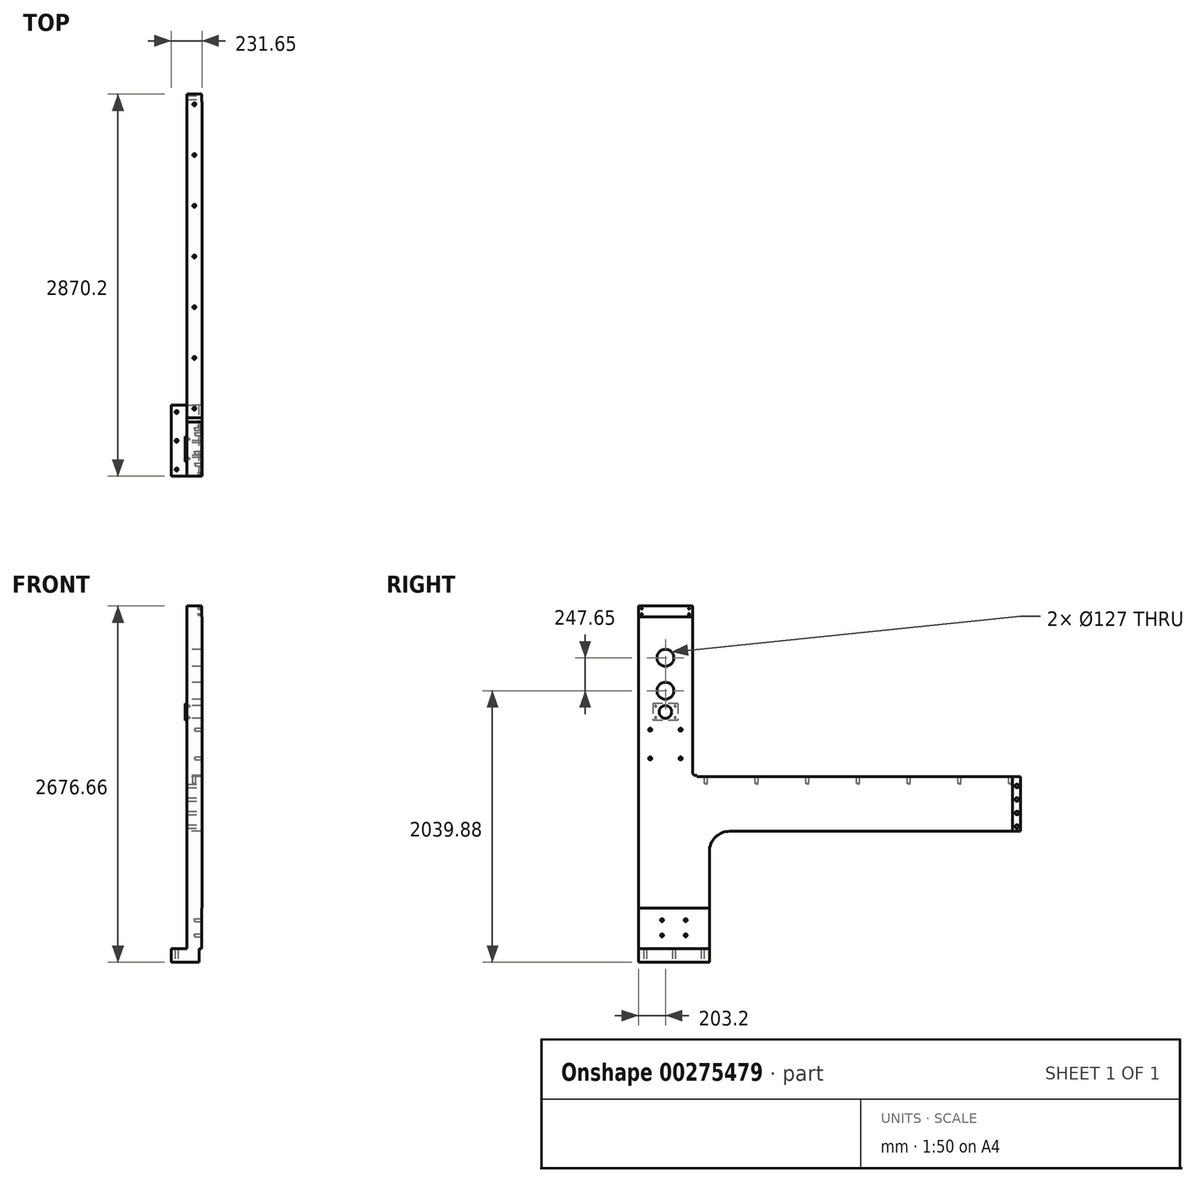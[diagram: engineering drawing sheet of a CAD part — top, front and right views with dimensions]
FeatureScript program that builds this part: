
annotation { "Feature Type Name" : "Feature", "Feature Type Description" : "" }
export const myFeature = defineFeature(function(context is Context, id is Id, definition is map)
    precondition{}
    {
        {
            var Q0;
            Q0=qCreatedBy(makeId("Right.planeOp"),FACE);
            var sketch = newSketch(context, id + "F0", { "sketchPlane" : qUnion([Q0])});
            skLineSegment(sketch, "E0", {"start": v(0, 1338.33) * mm, "end": v(0, -1338.33) * mm});
            skLineSegment(sketch, "E1.bottom", {"start": v(0, 1338.33) * mm, "end": v(406.4, 1338.33) * mm});
            skLineSegment(sketch, "E1.left", {"start": v(0, 1338.33) * mm, "end": v(0, -642.77) * mm});
            skLineSegment(sketch, "E1.right", {"start": v(406.4, 1338.33) * mm, "end": v(406.4, 90.42) * mm});
            skLineSegment(sketch, "E2", {"start": v(0, -1338.33) * mm, "end": v(2674.85, -1338.33) * mm, "construction": true});
            skLineSegment(sketch, "E3.0", {"start": v(0, -1236.73) * mm, "end": v(897.1, -1236.73) * mm, "construction": true});
            skLineSegment(sketch, "E4.bottom", {"start": v(0, -1236.73) * mm, "end": v(533.4, -1236.73) * mm});
            skLineSegment(sketch, "E4.top", {"start": v(406.4, 65.02) * mm, "end": v(438.15, 65.02) * mm});
            skLineSegment(sketch, "E4.left", {"start": v(0, -1236.73) * mm, "end": v(0, 65.02) * mm});
            skLineSegment(sketch, "E4.right", {"start": v(533.4, -1236.73) * mm, "end": v(533.4, -506.48) * mm});
            skLineSegment(sketch, "E5.bottom", {"start": v(431.8, 65.02) * mm, "end": v(438.15, 65.02) * mm});
            skLineSegment(sketch, "E5.top", {"start": v(685.8, -354.08) * mm, "end": v(2870.2, -354.08) * mm});
            skLineSegment(sketch, "E5.left", {"start": v(0, 65.02) * mm, "end": v(0, -354.08) * mm});
            skLineSegment(sketch, "E5.right", {"start": v(2870.2, 57.02) * mm, "end": v(2870.2, -354.08) * mm});
            skPoint(sketch, "E6.visualSharp", {"position": v(533.4, -354.08) * mm});
            skArc(sketch, "E6.filletArc", {"start": v(685.8, -354.08) * mm, "mid": v(578.04, -398.71) * mm, "end": v(533.4, -506.48) * mm});
            skPoint(sketch, "E7.visualSharp", {"position": v(406.4, 65.02) * mm});
            skArc(sketch, "E7.filletArc", {"start": v(406.4, 90.42) * mm, "mid": v(413.84, 72.46) * mm, "end": v(431.8, 65.02) * mm});
            skLineSegment(sketch, "E8.0", {"start": v(0, 701.55) * mm, "end": v(2674.85, 701.55) * mm, "construction": true});
            skLineSegment(sketch, "E9.0", {"start": v(0, 949.2) * mm, "end": v(2674.85, 949.2) * mm, "construction": true});
            skLineSegment(sketch, "E10", {"start": v(203.2, 1338.33) * mm, "end": v(203.2, -548.87) * mm, "construction": true});
            skCircle(sketch, "E11", {"center": v(203.2, 949.2) * mm, "radius": 63.5 * mm});
            skCircle(sketch, "E12", {"center": v(203.2, 701.55) * mm, "radius": 63.5 * mm});
            skLineSegment(sketch, "E13.0", {"start": v(438.15, 1338.33) * mm, "end": v(438.15, 701.55) * mm, "construction": true});
            skLineSegment(sketch, "E14.0", {"start": v(0, 57.02) * mm, "end": v(203.2, 57.02) * mm, "construction": true});
            skLineSegment(sketch, "E15.trimOffspring", {"start": v(438.15, 57.02) * mm, "end": v(2870.2, 57.02) * mm});
            skLineSegment(sketch, "E16.trimOffspring", {"start": v(438.15, 65.02) * mm, "end": v(438.15, 57.02) * mm});
            skSolve(sketch);
        }
        {
            var Q0;
            Q0 = qSketchRegion(id + "F0", true);
            extrude(context, id + "F1", {"entities" : qUnion([Q0]), "endBound" : BoundingType.SYMMETRIC, "depth" : 114.3 * mm});
        }
        {
            var Q0;
            Q0=makeQuery(id+"F1.opExtrude","CAP_FACE",FACE,{"disambiguationData":[OSD([sQuery(id+"F0.wireOp",EDGE,"E1.bottom"),sQuery(id+"F0.wireOp",EDGE,"E1.left"),sQuery(id+"F0.wireOp",EDGE,"E1.right"),sQuery(id+"F0.wireOp",EDGE,"E4.bottom"),sQuery(id+"F0.wireOp",EDGE,"E4.left"),sQuery(id+"F0.wireOp",EDGE,"E4.right"),sQuery(id+"F0.wireOp",EDGE,"E5.bottom"),sQuery(id+"F0.wireOp",EDGE,"E5.top"),sQuery(id+"F0.wireOp",EDGE,"E5.left"),sQuery(id+"F0.wireOp",EDGE,"E5.right"),sQuery(id+"F0.wireOp",EDGE,"E6.filletArc"),sQuery(id+"F0.wireOp",EDGE,"E7.filletArc"),sQuery(id+"F0.wireOp",EDGE,"E11"),sQuery(id+"F0.wireOp",EDGE,"E12"),sQuery(id+"F0.wireOp",EDGE,"E15.trimOffspring"),sQuery(id+"F0.wireOp",EDGE,"E16.trimOffspring")])],"isStart":false});
            var sketch = newSketch(context, id + "F2", { "sketchPlane" : qUnion([Q0])});
            skLineSegment(sketch, "E17.bottom", {"start": v(0, 1338.33) * mm, "end": v(406.4, 1338.33) * mm});
            skLineSegment(sketch, "E17.top", {"start": v(0, 1255.78) * mm, "end": v(406.4, 1255.78) * mm});
            skLineSegment(sketch, "E17.left", {"start": v(0, 1338.33) * mm, "end": v(0, 1255.78) * mm});
            skLineSegment(sketch, "E17.right", {"start": v(406.4, 1338.33) * mm, "end": v(406.4, 1255.78) * mm});
            skSolve(sketch);
        }
        {
            var Q0;
            Q0=makeQuery(id+"F2.imprint","IMPRINT",FACE,{"disambiguationData":[TD([[makeQuery(id+"F2.imprint","IMPRINT",EDGE,{"derivedFrom":sQuery(id+"F2.wireOp",EDGE,"E17.bottom")}),-1.0]])]});
            extrude(context, id + "F3", {"entities" : qUnion([Q0]), "operationType" : NewBodyOperationType.REMOVE, "oppositeDirection" : true, "depth" : 3.05 * mm});
        }
        {
            var Q0;
            Q0=makeQuery(id+"F3.boolean.opBoolean","COPY",FACE,{"derivedFrom":makeQuery(id+"F3.opExtrude","CAP_FACE",FACE,{"disambiguationData":[OSD([sQuery(id+"F2.wireOp",EDGE,"E17.bottom"),sQuery(id+"F2.wireOp",EDGE,"E17.top"),sQuery(id+"F2.wireOp",EDGE,"E17.left"),sQuery(id+"F2.wireOp",EDGE,"E17.right")])],"isStart":false})});
            var sketch = newSketch(context, id + "F4", { "sketchPlane" : qUnion([Q0])});
            skLineSegment(sketch, "E18", {"start": v(203.2, 1338.33) * mm, "end": v(203.2, 1255.78) * mm, "construction": true});
            skCircle(sketch, "E19.0", {"center": v(203.2, 949.2) * mm, "radius": 63.5 * mm, "construction": true});
            skLineSegment(sketch, "E20", {"start": v(203.2, 949.2) * mm, "end": v(580.51, 949.2) * mm, "construction": true});
            skLineSegment(sketch, "E21.0", {"start": v(25.4, 1276.22) * mm, "end": v(580.51, 1276.22) * mm, "construction": true});
            skLineSegment(sketch, "E22.0", {"start": v(25.4, 1320.67) * mm, "end": v(580.51, 1320.67) * mm, "construction": true});
            skLineSegment(sketch, "E23.0", {"start": v(25.4, 1338.33) * mm, "end": v(25.4, 1255.78) * mm, "construction": true});
            skPoint(sketch, "E24", {"position": v(25.4, 1320.67) * mm});
            skPoint(sketch, "E25", {"position": v(25.4, 1276.22) * mm});
            skPoint(sketch, "E26.MirrorP", {"position": v(381, 1320.67) * mm});
            skPoint(sketch, "E27.MirrorP", {"position": v(381, 1276.22) * mm});
            skSolve(sketch);
        }
        {
            var Q0;
            Q0=sQuery(id+"F4.wireOp",VERTEX,"E24");
            var Q1;
            Q1=sQuery(id+"F4.wireOp",VERTEX,"E25");
            var Q2;
            Q2=sQuery(id+"F4.wireOp",VERTEX,"E26.MirrorP");
            var Q3;
            Q3=sQuery(id+"F4.wireOp",VERTEX,"E27.MirrorP");
            var Q4;
            Q4=makeQuery(id+"F1.opExtrude","SWEPT_BODY",BODY,{"disambiguationData":[OSD([sQuery(id+"F0.wireOp",EDGE,"E1.bottom"),sQuery(id+"F0.wireOp",EDGE,"E1.left"),sQuery(id+"F0.wireOp",EDGE,"E1.right"),sQuery(id+"F0.wireOp",EDGE,"E4.bottom"),sQuery(id+"F0.wireOp",EDGE,"E4.left"),sQuery(id+"F0.wireOp",EDGE,"E4.right"),sQuery(id+"F0.wireOp",EDGE,"E5.bottom"),sQuery(id+"F0.wireOp",EDGE,"E5.top"),sQuery(id+"F0.wireOp",EDGE,"E5.left"),sQuery(id+"F0.wireOp",EDGE,"E5.right"),sQuery(id+"F0.wireOp",EDGE,"E6.filletArc"),sQuery(id+"F0.wireOp",EDGE,"E7.filletArc"),sQuery(id+"F0.wireOp",EDGE,"E11"),sQuery(id+"F0.wireOp",EDGE,"E12"),sQuery(id+"F0.wireOp",EDGE,"E15.trimOffspring"),sQuery(id+"F0.wireOp",EDGE,"E16.trimOffspring")])]});
            hole(context, id + "F5", {"style" : HoleStyle.SIMPLE, "endStyle" : HoleEndStyle.BLIND, "standardTappedOrClearance" : lookupTablePath({ "standard" : "ANSI", "engagement" : "75%", "pitch" : "13 tpi", "size" : "1/2", "type" : "Tapped" }), "standardBlindInLast" : lookupTablePath({ "standard" : "ANSI", "engagement" : "75%", "pitch" : "13 tpi", "size" : "1/2", "type" : "Tapped" }), "holeDiameter" : 10.72 * mm, "showTappedDepth" : true, "holeDepth" : 25.4 * mm, "tappedDepth" : 19.54 * mm, "tapClearance" : 3, "startFromSketch" : true, "locations" : qUnion([Q0, Q1, Q2, Q3]), "scope" : qUnion([Q4]), "majorDiameter" : 12.7 * mm});
        }
        {
            var Q0;
            Q0=makeQuery(id+"F1.opExtrude","CAP_FACE",FACE,{"disambiguationData":[OSD([sQuery(id+"F0.wireOp",EDGE,"E1.bottom"),sQuery(id+"F0.wireOp",EDGE,"E1.left"),sQuery(id+"F0.wireOp",EDGE,"E1.right"),sQuery(id+"F0.wireOp",EDGE,"E4.bottom"),sQuery(id+"F0.wireOp",EDGE,"E4.left"),sQuery(id+"F0.wireOp",EDGE,"E4.right"),sQuery(id+"F0.wireOp",EDGE,"E5.bottom"),sQuery(id+"F0.wireOp",EDGE,"E5.top"),sQuery(id+"F0.wireOp",EDGE,"E5.left"),sQuery(id+"F0.wireOp",EDGE,"E5.right"),sQuery(id+"F0.wireOp",EDGE,"E6.filletArc"),sQuery(id+"F0.wireOp",EDGE,"E7.filletArc"),sQuery(id+"F0.wireOp",EDGE,"E11"),sQuery(id+"F0.wireOp",EDGE,"E12"),sQuery(id+"F0.wireOp",EDGE,"E15.trimOffspring"),sQuery(id+"F0.wireOp",EDGE,"E16.trimOffspring")])],"isStart":true});
            var sketch = newSketch(context, id + "F6", { "sketchPlane" : qUnion([Q0])});
            skCircle(sketch, "E28.0", {"center": v(-203.2, 949.2) * mm, "radius": 63.5 * mm, "construction": true});
            skCircle(sketch, "E29.0", {"center": v(-203.2, 701.55) * mm, "radius": 63.5 * mm, "construction": true});
            skCircle(sketch, "E30", {"center": v(-203.2, 949.2) * mm, "radius": 104.78 * mm});
            skCircle(sketch, "E31", {"center": v(-203.2, 701.55) * mm, "radius": 104.78 * mm});
            skSolve(sketch);
        }
        {
            var Q0;
            Q0=makeQuery(id+"F1.opExtrude","CAP_FACE",FACE,{"disambiguationData":[OSD([sQuery(id+"F0.wireOp",EDGE,"E1.bottom"),sQuery(id+"F0.wireOp",EDGE,"E1.left"),sQuery(id+"F0.wireOp",EDGE,"E1.right"),sQuery(id+"F0.wireOp",EDGE,"E4.bottom"),sQuery(id+"F0.wireOp",EDGE,"E4.left"),sQuery(id+"F0.wireOp",EDGE,"E4.right"),sQuery(id+"F0.wireOp",EDGE,"E5.bottom"),sQuery(id+"F0.wireOp",EDGE,"E5.top"),sQuery(id+"F0.wireOp",EDGE,"E5.left"),sQuery(id+"F0.wireOp",EDGE,"E5.right"),sQuery(id+"F0.wireOp",EDGE,"E6.filletArc"),sQuery(id+"F0.wireOp",EDGE,"E7.filletArc"),sQuery(id+"F0.wireOp",EDGE,"E11"),sQuery(id+"F0.wireOp",EDGE,"E12"),sQuery(id+"F0.wireOp",EDGE,"E15.trimOffspring"),sQuery(id+"F0.wireOp",EDGE,"E16.trimOffspring")])],"isStart":false});
            var sketch = newSketch(context, id + "F7", { "sketchPlane" : qUnion([Q0])});
            skCircle(sketch, "E32.0", {"center": v(203.2, 701.55) * mm, "radius": 63.5 * mm, "construction": true});
            skLineSegment(sketch, "E33", {"start": v(203.2, 701.55) * mm, "end": v(203.2, -117.25) * mm, "construction": true});
            skLineSegment(sketch, "E34", {"start": v(203.2, 701.55) * mm, "end": v(767.73, 701.55) * mm, "construction": true});
            skLineSegment(sketch, "E35.0", {"start": v(203.2, 409.45) * mm, "end": v(767.73, 409.45) * mm, "construction": true});
            skLineSegment(sketch, "E36.0", {"start": v(203.2, 193.55) * mm, "end": v(767.73, 193.55) * mm, "construction": true});
            skLineSegment(sketch, "E37.0", {"start": v(317.5, 701.55) * mm, "end": v(317.5, -117.25) * mm, "construction": true});
            skPoint(sketch, "E38", {"position": v(317.5, 409.45) * mm});
            skPoint(sketch, "E39", {"position": v(317.5, 193.55) * mm});
            skPoint(sketch, "E40.MirrorP", {"position": v(88.9, 409.45) * mm});
            skPoint(sketch, "E41.MirrorP", {"position": v(88.9, 193.55) * mm});
            skSolve(sketch);
        }
        {
            var Q0;
            Q0=sQuery(id+"F7.wireOp",VERTEX,"E40.MirrorP");
            var Q1;
            Q1=sQuery(id+"F7.wireOp",VERTEX,"E38");
            var Q2;
            Q2=sQuery(id+"F7.wireOp",VERTEX,"E41.MirrorP");
            var Q3;
            Q3=sQuery(id+"F7.wireOp",VERTEX,"E39");
            var Q4;
            Q4=makeQuery(id+"F1.opExtrude","SWEPT_BODY",BODY,{"disambiguationData":[OSD([sQuery(id+"F0.wireOp",EDGE,"E1.bottom"),sQuery(id+"F0.wireOp",EDGE,"E1.left"),sQuery(id+"F0.wireOp",EDGE,"E1.right"),sQuery(id+"F0.wireOp",EDGE,"E4.bottom"),sQuery(id+"F0.wireOp",EDGE,"E4.left"),sQuery(id+"F0.wireOp",EDGE,"E4.right"),sQuery(id+"F0.wireOp",EDGE,"E5.bottom"),sQuery(id+"F0.wireOp",EDGE,"E5.top"),sQuery(id+"F0.wireOp",EDGE,"E5.left"),sQuery(id+"F0.wireOp",EDGE,"E5.right"),sQuery(id+"F0.wireOp",EDGE,"E6.filletArc"),sQuery(id+"F0.wireOp",EDGE,"E7.filletArc"),sQuery(id+"F0.wireOp",EDGE,"E11"),sQuery(id+"F0.wireOp",EDGE,"E12"),sQuery(id+"F0.wireOp",EDGE,"E15.trimOffspring"),sQuery(id+"F0.wireOp",EDGE,"E16.trimOffspring")])]});
            hole(context, id + "F8", {"style" : HoleStyle.SIMPLE, "endStyle" : HoleEndStyle.BLIND, "standardTappedOrClearance" : lookupTablePath({ "standard" : "ANSI", "engagement" : "75%", "pitch" : "8 tpi", "size" : "1", "type" : "Tapped" }), "standardBlindInLast" : lookupTablePath({ "standard" : "ANSI", "engagement" : "75%", "pitch" : "8 tpi", "size" : "1", "type" : "Tapped" }), "holeDiameter" : 22.22 * mm, "showTappedDepth" : true, "holeDepth" : 50.8 * mm, "tappedDepth" : 41.27 * mm, "tapClearance" : 3, "startFromSketch" : true, "locations" : qUnion([Q0, Q1, Q2, Q3]), "scope" : qUnion([Q4]), "majorDiameter" : 25.4 * mm});
        }
        {
            var Q0;
            Q0=makeQuery(id+"F1.opExtrude","CAP_FACE",FACE,{"disambiguationData":[OSD([sQuery(id+"F0.wireOp",EDGE,"E1.bottom"),sQuery(id+"F0.wireOp",EDGE,"E1.left"),sQuery(id+"F0.wireOp",EDGE,"E1.right"),sQuery(id+"F0.wireOp",EDGE,"E4.bottom"),sQuery(id+"F0.wireOp",EDGE,"E4.left"),sQuery(id+"F0.wireOp",EDGE,"E4.right"),sQuery(id+"F0.wireOp",EDGE,"E5.bottom"),sQuery(id+"F0.wireOp",EDGE,"E5.top"),sQuery(id+"F0.wireOp",EDGE,"E5.left"),sQuery(id+"F0.wireOp",EDGE,"E5.right"),sQuery(id+"F0.wireOp",EDGE,"E6.filletArc"),sQuery(id+"F0.wireOp",EDGE,"E7.filletArc"),sQuery(id+"F0.wireOp",EDGE,"E11"),sQuery(id+"F0.wireOp",EDGE,"E12"),sQuery(id+"F0.wireOp",EDGE,"E15.trimOffspring"),sQuery(id+"F0.wireOp",EDGE,"E16.trimOffspring")])],"isStart":false});
            var sketch = newSketch(context, id + "F9", { "sketchPlane" : qUnion([Q0])});
            skLineSegment(sketch, "E42.bottom", {"start": v(2870.2, 57.02) * mm, "end": v(2813.05, 57.02) * mm});
            skLineSegment(sketch, "E42.top", {"start": v(2870.2, -354.08) * mm, "end": v(2813.05, -354.08) * mm});
            skLineSegment(sketch, "E42.left", {"start": v(2870.2, 57.02) * mm, "end": v(2870.2, -354.08) * mm});
            skLineSegment(sketch, "E42.right", {"start": v(2813.05, 57.02) * mm, "end": v(2813.05, -354.08) * mm});
            skSolve(sketch);
        }
        {
            var Q0;
            Q0 = qSketchRegion(id + "F9", true);
            extrude(context, id + "F10", {"entities" : qUnion([Q0]), "operationType" : NewBodyOperationType.REMOVE, "oppositeDirection" : true, "depth" : 3.17 * mm});
        }
        {
            var Q0;
            Q0=makeQuery(id+"F10.boolean.opBoolean","COPY",FACE,{"derivedFrom":makeQuery(id+"F10.opExtrude","CAP_FACE",FACE,{"disambiguationData":[OSD([sQuery(id+"F9.wireOp",EDGE,"E42.bottom"),sQuery(id+"F9.wireOp",EDGE,"E42.top"),sQuery(id+"F9.wireOp",EDGE,"E42.left"),sQuery(id+"F9.wireOp",EDGE,"E42.right")])],"isStart":false})});
            var sketch = newSketch(context, id + "F11", { "sketchPlane" : qUnion([Q0])});
            skLineSegment(sketch, "E43.0", {"start": v(2813.05, 57.02) * mm, "end": v(2870.2, 57.02) * mm, "construction": true});
            skCircle(sketch, "E44.0", {"center": v(203.2, 701.55) * mm, "radius": 63.5 * mm, "construction": true});
            skLineSegment(sketch, "E45", {"start": v(203.2, 701.55) * mm, "end": v(203.2, -538.92) * mm, "construction": true});
            skLineSegment(sketch, "E46.0", {"start": v(2844.8, 701.55) * mm, "end": v(2844.8, -538.92) * mm, "construction": true});
            skLineSegment(sketch, "E47.0", {"start": v(2813.05, -12.83) * mm, "end": v(2870.2, -12.83) * mm, "construction": true});
            skPoint(sketch, "E48", {"position": v(2844.8, -12.83) * mm});
            skPoint(sketch, "E49.0.1.0", {"position": v(2844.8, -114.43) * mm});
            skPoint(sketch, "E49.0.2.0", {"position": v(2844.8, -216.03) * mm});
            skPoint(sketch, "E49.0.3.0", {"position": v(2844.8, -317.63) * mm});
            skLineSegment(sketch, "E49.direction1", {"start": v(2844.8, -12.83) * mm, "end": v(2870.2, -12.83) * mm, "construction": true});
            skLineSegment(sketch, "E49.direction2", {"start": v(2844.8, -12.83) * mm, "end": v(2844.8, -114.43) * mm, "construction": true});
            skSolve(sketch);
        }
        {
            var Q0;
            Q0=sQuery(id+"F11.wireOp",VERTEX,"E48");
            var Q1;
            Q1=sQuery(id+"F11.wireOp",VERTEX,"E49.0.1.0");
            var Q2;
            Q2=sQuery(id+"F11.wireOp",VERTEX,"E49.0.2.0");
            var Q3;
            Q3=sQuery(id+"F11.wireOp",VERTEX,"E49.0.3.0");
            var Q4;
            Q4=makeQuery(id+"F1.opExtrude","SWEPT_BODY",BODY,{"disambiguationData":[OSD([sQuery(id+"F0.wireOp",EDGE,"E1.bottom"),sQuery(id+"F0.wireOp",EDGE,"E1.left"),sQuery(id+"F0.wireOp",EDGE,"E1.right"),sQuery(id+"F0.wireOp",EDGE,"E4.bottom"),sQuery(id+"F0.wireOp",EDGE,"E4.left"),sQuery(id+"F0.wireOp",EDGE,"E4.right"),sQuery(id+"F0.wireOp",EDGE,"E5.bottom"),sQuery(id+"F0.wireOp",EDGE,"E5.top"),sQuery(id+"F0.wireOp",EDGE,"E5.left"),sQuery(id+"F0.wireOp",EDGE,"E5.right"),sQuery(id+"F0.wireOp",EDGE,"E6.filletArc"),sQuery(id+"F0.wireOp",EDGE,"E7.filletArc"),sQuery(id+"F0.wireOp",EDGE,"E11"),sQuery(id+"F0.wireOp",EDGE,"E12"),sQuery(id+"F0.wireOp",EDGE,"E15.trimOffspring"),sQuery(id+"F0.wireOp",EDGE,"E16.trimOffspring")])]});
            hole(context, id + "F12", {"style" : HoleStyle.SIMPLE, "endStyle" : HoleEndStyle.THROUGH, "holeDiameter" : 26.92 * mm, "tappedDepth" : 41.27 * mm, "tapClearance" : 3, "startFromSketch" : true, "locations" : qUnion([Q0, Q1, Q2, Q3]), "scope" : qUnion([Q4])});
        }
        {
            var Q0;
            Q0=makeQuery(id+"F1.opExtrude","SWEPT_FACE",FACE,{"disambiguationData":[OSD([sQuery(id+"F0.wireOp",EDGE,"E15.trimOffspring")])]});
            var sketch = newSketch(context, id + "F13", { "sketchPlane" : qUnion([Q0])});
            skLineSegment(sketch, "E50", {"start": v(0, -474.51) * mm, "end": v(0, 3159.2) * mm, "construction": true});
            skLineSegment(sketch, "E51.0", {"start": v(-31.75, 98.43) * mm, "end": v(-31.75, 307.98) * mm, "construction": true});
            skLineSegment(sketch, "E52", {"start": v(-31.75, 203.2) * mm, "end": v(158.49, 203.2) * mm, "construction": true});
            skLineSegment(sketch, "E53.0", {"start": v(-31.75, 508) * mm, "end": v(158.49, 508) * mm, "construction": true});
            skPoint(sketch, "E54", {"position": v(0, 508) * mm});
            skPoint(sketch, "E55.0.1.0", {"position": v(0, 889) * mm});
            skPoint(sketch, "E55.0.2.0", {"position": v(0, 1270) * mm});
            skPoint(sketch, "E55.0.3.0", {"position": v(0, 1651) * mm});
            skPoint(sketch, "E55.0.4.0", {"position": v(0, 2032) * mm});
            skPoint(sketch, "E55.0.5.0", {"position": v(0, 2413) * mm});
            skPoint(sketch, "E55.0.6.0", {"position": v(0, 2794) * mm});
            skLineSegment(sketch, "E55.direction1", {"start": v(0, 508) * mm, "end": v(25.4, 508) * mm, "construction": true});
            skLineSegment(sketch, "E55.direction2", {"start": v(0, 508) * mm, "end": v(0, 889) * mm, "construction": true});
            skSolve(sketch);
        }
        {
            var Q0;
            Q0=sQuery(id+"F13.wireOp",VERTEX,"E54");
            var Q1;
            Q1=sQuery(id+"F13.wireOp",VERTEX,"E55.0.1.0");
            var Q2;
            Q2=sQuery(id+"F13.wireOp",VERTEX,"E55.0.2.0");
            var Q3;
            Q3=sQuery(id+"F13.wireOp",VERTEX,"E55.0.3.0");
            var Q4;
            Q4=sQuery(id+"F13.wireOp",VERTEX,"E55.0.4.0");
            var Q5;
            Q5=sQuery(id+"F13.wireOp",VERTEX,"E55.0.5.0");
            var Q6;
            Q6=sQuery(id+"F13.wireOp",VERTEX,"E55.0.6.0");
            var Q7;
            Q7=makeQuery(id+"F1.opExtrude","SWEPT_BODY",BODY,{"disambiguationData":[OSD([sQuery(id+"F0.wireOp",EDGE,"E1.bottom"),sQuery(id+"F0.wireOp",EDGE,"E1.left"),sQuery(id+"F0.wireOp",EDGE,"E1.right"),sQuery(id+"F0.wireOp",EDGE,"E4.bottom"),sQuery(id+"F0.wireOp",EDGE,"E4.left"),sQuery(id+"F0.wireOp",EDGE,"E4.right"),sQuery(id+"F0.wireOp",EDGE,"E5.bottom"),sQuery(id+"F0.wireOp",EDGE,"E5.top"),sQuery(id+"F0.wireOp",EDGE,"E5.left"),sQuery(id+"F0.wireOp",EDGE,"E5.right"),sQuery(id+"F0.wireOp",EDGE,"E6.filletArc"),sQuery(id+"F0.wireOp",EDGE,"E7.filletArc"),sQuery(id+"F0.wireOp",EDGE,"E11"),sQuery(id+"F0.wireOp",EDGE,"E12"),sQuery(id+"F0.wireOp",EDGE,"E15.trimOffspring"),sQuery(id+"F0.wireOp",EDGE,"E16.trimOffspring")])]});
            hole(context, id + "F14", {"style" : HoleStyle.SIMPLE, "endStyle" : HoleEndStyle.BLIND, "standardTappedOrClearance" : lookupTablePath({ "standard" : "ANSI", "engagement" : "75%", "pitch" : "8 tpi", "size" : "1", "type" : "Tapped" }), "standardBlindInLast" : lookupTablePath({ "standard" : "ANSI", "engagement" : "75%", "pitch" : "8 tpi", "size" : "1", "type" : "Tapped" }), "holeDiameter" : 22.22 * mm, "showTappedDepth" : true, "holeDepth" : 50.8 * mm, "tappedDepth" : 41.27 * mm, "tapClearance" : 3, "startFromSketch" : true, "locations" : qUnion([Q0, Q1, Q2, Q3, Q4, Q5, Q6]), "scope" : qUnion([Q7]), "majorDiameter" : 25.4 * mm});
        }
        {
            var Q0;
            Q0=makeQuery(id+"F1.opExtrude","CAP_FACE",FACE,{"disambiguationData":[OSD([sQuery(id+"F0.wireOp",EDGE,"E1.bottom"),sQuery(id+"F0.wireOp",EDGE,"E1.left"),sQuery(id+"F0.wireOp",EDGE,"E1.right"),sQuery(id+"F0.wireOp",EDGE,"E4.bottom"),sQuery(id+"F0.wireOp",EDGE,"E4.left"),sQuery(id+"F0.wireOp",EDGE,"E4.right"),sQuery(id+"F0.wireOp",EDGE,"E5.bottom"),sQuery(id+"F0.wireOp",EDGE,"E5.top"),sQuery(id+"F0.wireOp",EDGE,"E5.left"),sQuery(id+"F0.wireOp",EDGE,"E5.right"),sQuery(id+"F0.wireOp",EDGE,"E6.filletArc"),sQuery(id+"F0.wireOp",EDGE,"E7.filletArc"),sQuery(id+"F0.wireOp",EDGE,"E11"),sQuery(id+"F0.wireOp",EDGE,"E12"),sQuery(id+"F0.wireOp",EDGE,"E15.trimOffspring"),sQuery(id+"F0.wireOp",EDGE,"E16.trimOffspring")])],"isStart":false});
            var sketch = newSketch(context, id + "F15", { "sketchPlane" : qUnion([Q0])});
            skLineSegment(sketch, "E56.bottom", {"start": v(0, -1236.73) * mm, "end": v(533.4, -1236.73) * mm});
            skLineSegment(sketch, "E56.top", {"start": v(0, -931.93) * mm, "end": v(533.4, -931.93) * mm});
            skLineSegment(sketch, "E56.left", {"start": v(0, -1236.73) * mm, "end": v(0, -931.93) * mm});
            skLineSegment(sketch, "E56.right", {"start": v(533.4, -1236.73) * mm, "end": v(533.4, -931.93) * mm});
            skSolve(sketch);
        }
        {
            var Q0;
            Q0=makeQuery(id+"F15.imprint","IMPRINT",FACE,{"disambiguationData":[TD([[makeQuery(id+"F15.imprint","IMPRINT",EDGE,{"derivedFrom":sQuery(id+"F15.wireOp",EDGE,"E56.bottom")}),1.0]])]});
            extrude(context, id + "F16", {"entities" : qUnion([Q0]), "operationType" : NewBodyOperationType.REMOVE, "oppositeDirection" : true, "depth" : 3.05 * mm});
        }
        {
            var Q0;
            Q0=makeQuery(id+"F16.boolean.opBoolean","COPY",FACE,{"derivedFrom":makeQuery(id+"F16.opExtrude","CAP_FACE",FACE,{"disambiguationData":[OSD([sQuery(id+"F15.wireOp",EDGE,"E56.bottom"),sQuery(id+"F15.wireOp",EDGE,"E56.top"),sQuery(id+"F15.wireOp",EDGE,"E56.left"),sQuery(id+"F15.wireOp",EDGE,"E56.right")])],"isStart":false})});
            var sketch = newSketch(context, id + "F17", { "sketchPlane" : qUnion([Q0])});
            skLineSegment(sketch, "E57.0", {"start": v(0, -1236.73) * mm, "end": v(533.4, -1236.73) * mm, "construction": true});
            skLineSegment(sketch, "E58", {"start": v(266.7, -1236.73) * mm, "end": v(266.7, -931.93) * mm, "construction": true});
            skLineSegment(sketch, "E59.0", {"start": v(0, -1135.13) * mm, "end": v(533.4, -1135.13) * mm, "construction": true});
            skLineSegment(sketch, "E60.0", {"start": v(0, -1020.83) * mm, "end": v(533.4, -1020.83) * mm, "construction": true});
            skLineSegment(sketch, "E61.0", {"start": v(177.8, -1236.73) * mm, "end": v(177.8, -931.93) * mm, "construction": true});
            skPoint(sketch, "E62", {"position": v(177.8, -1020.83) * mm});
            skPoint(sketch, "E63", {"position": v(177.8, -1135.13) * mm});
            skPoint(sketch, "E64.MirrorP", {"position": v(355.6, -1020.83) * mm});
            skPoint(sketch, "E65.MirrorP", {"position": v(355.6, -1135.13) * mm});
            skSolve(sketch);
        }
        {
            var Q0;
            Q0=sQuery(id+"F17.wireOp",VERTEX,"E62");
            var Q1;
            Q1=sQuery(id+"F17.wireOp",VERTEX,"E64.MirrorP");
            var Q2;
            Q2=sQuery(id+"F17.wireOp",VERTEX,"E65.MirrorP");
            var Q3;
            Q3=sQuery(id+"F17.wireOp",VERTEX,"E63");
            var Q4;
            Q4=makeQuery(id+"F1.opExtrude","SWEPT_BODY",BODY,{"disambiguationData":[OSD([sQuery(id+"F0.wireOp",EDGE,"E1.bottom"),sQuery(id+"F0.wireOp",EDGE,"E1.left"),sQuery(id+"F0.wireOp",EDGE,"E1.right"),sQuery(id+"F0.wireOp",EDGE,"E4.bottom"),sQuery(id+"F0.wireOp",EDGE,"E4.left"),sQuery(id+"F0.wireOp",EDGE,"E4.right"),sQuery(id+"F0.wireOp",EDGE,"E5.bottom"),sQuery(id+"F0.wireOp",EDGE,"E5.top"),sQuery(id+"F0.wireOp",EDGE,"E5.left"),sQuery(id+"F0.wireOp",EDGE,"E5.right"),sQuery(id+"F0.wireOp",EDGE,"E6.filletArc"),sQuery(id+"F0.wireOp",EDGE,"E7.filletArc"),sQuery(id+"F0.wireOp",EDGE,"E11"),sQuery(id+"F0.wireOp",EDGE,"E12"),sQuery(id+"F0.wireOp",EDGE,"E15.trimOffspring"),sQuery(id+"F0.wireOp",EDGE,"E16.trimOffspring")])]});
            hole(context, id + "F18", {"style" : HoleStyle.SIMPLE, "endStyle" : HoleEndStyle.BLIND, "standardTappedOrClearance" : lookupTablePath({ "standard" : "ANSI", "engagement" : "75%", "pitch" : "8 tpi", "size" : "1", "type" : "Tapped" }), "standardBlindInLast" : lookupTablePath({ "standard" : "ANSI", "engagement" : "75%", "pitch" : "8 tpi", "size" : "1", "type" : "Tapped" }), "holeDiameter" : 22.22 * mm, "showTappedDepth" : true, "holeDepth" : 50.8 * mm, "tappedDepth" : 41.27 * mm, "tapClearance" : 3, "startFromSketch" : true, "locations" : qUnion([Q0, Q1, Q2, Q3]), "scope" : qUnion([Q4]), "majorDiameter" : 25.4 * mm});
        }
        {
            var Q0;
            Q0=makeQuery(id+"F16.boolean.opBoolean","COPY",FACE,{"derivedFrom":makeQuery(id+"F16.opExtrude","CAP_FACE",FACE,{"disambiguationData":[OSD([sQuery(id+"F15.wireOp",EDGE,"E56.bottom"),sQuery(id+"F15.wireOp",EDGE,"E56.top"),sQuery(id+"F15.wireOp",EDGE,"E56.left"),sQuery(id+"F15.wireOp",EDGE,"E56.right")])],"isStart":false})});
            cPlane(context, id + "F19", {"entities" : qUnion([Q0]), "cplaneType" : CPlaneType.OFFSET, "offset" : 19.05 * mm, "oppositeDirection" : true, "width" : 152.4 * mm, "height" : 152.4 * mm});
        }
        {
            var Q0;
            Q0=qCreatedBy(id+"F19.planeOp",FACE);
            var sketch = newSketch(context, id + "F20", { "sketchPlane" : qUnion([Q0])});
            skLineSegment(sketch, "E66.0", {"start": v(0, -1236.73) * mm, "end": v(533.4, -1236.73) * mm});
            skLineSegment(sketch, "E67.top", {"start": v(0, -1338.33) * mm, "end": v(533.4, -1338.33) * mm});
            skLineSegment(sketch, "E67.left", {"start": v(0, -1236.73) * mm, "end": v(0, -1338.33) * mm});
            skLineSegment(sketch, "E67.right", {"start": v(533.4, -1236.73) * mm, "end": v(533.4, -1338.33) * mm});
            skSolve(sketch);
        }
        {
            var Q0;
            Q0=makeQuery(id+"F20.imprint","IMPRINT",FACE,{"disambiguationData":[TD([[makeQuery(id+"F20.imprint","IMPRINT",EDGE,{"derivedFrom":sQuery(id+"F20.wireOp",EDGE,"E66.0")}),-1.0]])]});
            extrude(context, id + "F21", {"entities" : qUnion([Q0]), "operationType" : NewBodyOperationType.ADD, "oppositeDirection" : true, "depth" : 209.55 * mm});
        }
        {
            var Q0;
            Q0=makeQuery(id+"F21.opExtrude","SWEPT_FACE",FACE,{"disambiguationData":[OSD([sQuery(id+"F20.wireOp",EDGE,"E67.top")])]});
            var sketch = newSketch(context, id + "F22", { "sketchPlane" : qUnion([Q0])});
            skLineSegment(sketch, "E68.0", {"start": v(54.1, 0) * mm, "end": v(54.1, -533.4) * mm, "construction": true});
            skLineSegment(sketch, "E69.0", {"start": v(-133.35, 0) * mm, "end": v(-133.35, -533.4) * mm, "construction": true});
            skLineSegment(sketch, "E70", {"start": v(-133.35, -266.7) * mm, "end": v(-250.55, -266.7) * mm, "construction": true});
            skLineSegment(sketch, "E71.0", {"start": v(-133.35, -482.6) * mm, "end": v(-250.55, -482.6) * mm, "construction": true});
            skPoint(sketch, "E72", {"position": v(-133.35, -482.6) * mm});
            skPoint(sketch, "E73", {"position": v(-133.35, -266.7) * mm});
            skPoint(sketch, "E74.MirrorP", {"position": v(-133.35, -50.8) * mm});
            skSolve(sketch);
        }
        {
            var Q0;
            Q0=sQuery(id+"F22.wireOp",VERTEX,"E72");
            var Q1;
            Q1=sQuery(id+"F22.wireOp",VERTEX,"E73");
            var Q2;
            Q2=sQuery(id+"F22.wireOp",VERTEX,"E74.MirrorP");
            var Q3;
            Q3=makeQuery(id+"F1.opExtrude","SWEPT_BODY",BODY,{"disambiguationData":[OSD([sQuery(id+"F0.wireOp",EDGE,"E1.bottom"),sQuery(id+"F0.wireOp",EDGE,"E1.left"),sQuery(id+"F0.wireOp",EDGE,"E1.right"),sQuery(id+"F0.wireOp",EDGE,"E4.bottom"),sQuery(id+"F0.wireOp",EDGE,"E4.left"),sQuery(id+"F0.wireOp",EDGE,"E4.right"),sQuery(id+"F0.wireOp",EDGE,"E5.bottom"),sQuery(id+"F0.wireOp",EDGE,"E5.top"),sQuery(id+"F0.wireOp",EDGE,"E5.left"),sQuery(id+"F0.wireOp",EDGE,"E5.right"),sQuery(id+"F0.wireOp",EDGE,"E6.filletArc"),sQuery(id+"F0.wireOp",EDGE,"E7.filletArc"),sQuery(id+"F0.wireOp",EDGE,"E11"),sQuery(id+"F0.wireOp",EDGE,"E12"),sQuery(id+"F0.wireOp",EDGE,"E15.trimOffspring"),sQuery(id+"F0.wireOp",EDGE,"E16.trimOffspring")])]});
            hole(context, id + "F23", {"style" : HoleStyle.SIMPLE, "endStyle" : HoleEndStyle.THROUGH, "standardTappedOrClearance" : lookupTablePath({ "standard" : "ANSI", "engagement" : "75%", "pitch" : "8 tpi", "size" : "1", "type" : "Tapped" }), "standardBlindInLast" : lookupTablePath({ "standard" : "ANSI", "engagement" : "75%", "pitch" : "8 tpi", "size" : "1", "type" : "Tapped" }), "holeDiameter" : 22.22 * mm, "showTappedDepth" : true, "tappedDepth" : 41.27 * mm, "tapClearance" : 3, "startFromSketch" : true, "locations" : qUnion([Q0, Q1, Q2]), "scope" : qUnion([Q3]), "majorDiameter" : 25.4 * mm});
        }
        {
            var Q0;
            Q0=makeQuery(id+"F1.opExtrude","CAP_FACE",FACE,{"disambiguationData":[OSD([sQuery(id+"F0.wireOp",EDGE,"E1.bottom"),sQuery(id+"F0.wireOp",EDGE,"E1.left"),sQuery(id+"F0.wireOp",EDGE,"E1.right"),sQuery(id+"F0.wireOp",EDGE,"E4.bottom"),sQuery(id+"F0.wireOp",EDGE,"E4.left"),sQuery(id+"F0.wireOp",EDGE,"E4.right"),sQuery(id+"F0.wireOp",EDGE,"E5.bottom"),sQuery(id+"F0.wireOp",EDGE,"E5.top"),sQuery(id+"F0.wireOp",EDGE,"E5.left"),sQuery(id+"F0.wireOp",EDGE,"E5.right"),sQuery(id+"F0.wireOp",EDGE,"E6.filletArc"),sQuery(id+"F0.wireOp",EDGE,"E7.filletArc"),sQuery(id+"F0.wireOp",EDGE,"E11"),sQuery(id+"F0.wireOp",EDGE,"E12"),sQuery(id+"F0.wireOp",EDGE,"E15.trimOffspring"),sQuery(id+"F0.wireOp",EDGE,"E16.trimOffspring")])],"isStart":false});
            var sketch = newSketch(context, id + "F24", { "sketchPlane" : qUnion([Q0])});
            skCircle(sketch, "E75.0", {"center": v(203.2, 701.55) * mm, "radius": 63.5 * mm, "construction": true});
            skLineSegment(sketch, "E76", {"start": v(203.2, 701.55) * mm, "end": v(693.11, 701.55) * mm, "construction": true});
            skLineSegment(sketch, "E77.0", {"start": v(203.2, 504.7) * mm, "end": v(688.88, 504.7) * mm, "construction": true});
            skLineSegment(sketch, "E78.bottom", {"start": v(688.88, 504.7) * mm, "end": v(-225.52, 504.7) * mm});
            skLineSegment(sketch, "E78.top", {"start": v(688.88, 111) * mm, "end": v(-225.52, 111) * mm});
            skLineSegment(sketch, "E78.left", {"start": v(688.88, 504.7) * mm, "end": v(688.88, 111) * mm});
            skLineSegment(sketch, "E78.right", {"start": v(-225.52, 504.7) * mm, "end": v(-225.52, 111) * mm});
            skSolve(sketch);
        }
        {
            var Q0;
            {var subQ0=sQuery(id+"F24.wireOp",EDGE,"E78.right");Q0=makeQuery(id+"F24.imprint","IMPRINT",FACE,{"disambiguationData":[TD([[makeQuery(id+"F24.imprint","IMPRINT",EDGE,{"derivedFrom":subQ0}),1.0]])]});}
            var Q1;
            Q1=makeQuery(id+"F24.imprint","IMPRINT",FACE,{"disambiguationData":[TD([[makeQuery(id+"F24.imprint","IMPRINT",EDGE,{"derivedFrom":makeQuery(id+"F8.hole-0.boolean.opBoolean","COPY",EDGE,{"derivedFrom":makeQuery(id+"F8.hole-0.opRevolve","SWEPT_EDGE",EDGE,{"disambiguationData":[OSD([sQuery(id+"F8.hole-0.sketch.wireOp",EDGE,"core_line_2"),sQuery(id+"F8.hole-0.sketch.wireOp",EDGE,"core_line_3")])]})})}),-1.0]])]});
            var Q2;
            {var subQ0=sQuery(id+"F24.wireOp",EDGE,"E78.left");Q2=makeQuery(id+"F24.imprint","IMPRINT",FACE,{"disambiguationData":[TD([[makeQuery(id+"F24.imprint","IMPRINT",EDGE,{"derivedFrom":subQ0}),-1.0]])]});}
            extrude(context, id + "F25", {"entities" : qUnion([Q0, Q1, Q2]), "operationType" : NewBodyOperationType.REMOVE, "oppositeDirection" : true, "depth" : 3.05 * mm});
        }
        {
            var Q0;
            Q0=makeQuery(id+"F1.opExtrude","CAP_FACE",FACE,{"disambiguationData":[OSD([sQuery(id+"F0.wireOp",EDGE,"E1.bottom"),sQuery(id+"F0.wireOp",EDGE,"E1.left"),sQuery(id+"F0.wireOp",EDGE,"E1.right"),sQuery(id+"F0.wireOp",EDGE,"E4.bottom"),sQuery(id+"F0.wireOp",EDGE,"E4.left"),sQuery(id+"F0.wireOp",EDGE,"E4.right"),sQuery(id+"F0.wireOp",EDGE,"E5.bottom"),sQuery(id+"F0.wireOp",EDGE,"E5.top"),sQuery(id+"F0.wireOp",EDGE,"E5.left"),sQuery(id+"F0.wireOp",EDGE,"E5.right"),sQuery(id+"F0.wireOp",EDGE,"E6.filletArc"),sQuery(id+"F0.wireOp",EDGE,"E7.filletArc"),sQuery(id+"F0.wireOp",EDGE,"E11"),sQuery(id+"F0.wireOp",EDGE,"E12"),sQuery(id+"F0.wireOp",EDGE,"E15.trimOffspring"),sQuery(id+"F0.wireOp",EDGE,"E16.trimOffspring")])],"isStart":true});
            var sketch = newSketch(context, id + "F26", { "sketchPlane" : qUnion([Q0])});
            skLineSegment(sketch, "E79", {"start": v(-203.2, 949.2) * mm, "end": v(-203.2, 244.96) * mm, "construction": true});
            skCircle(sketch, "E80.0", {"center": v(-203.2, 949.2) * mm, "radius": 63.5 * mm, "construction": true});
            skCircle(sketch, "E81.0", {"center": v(-203.2, 701.55) * mm, "radius": 63.5 * mm, "construction": true});
            skLineSegment(sketch, "E82", {"start": v(-203.2, 701.55) * mm, "end": v(-889.9, 701.55) * mm, "construction": true});
            skLineSegment(sketch, "E83.0", {"start": v(-203.2, 542.8) * mm, "end": v(-889.9, 542.8) * mm, "construction": true});
            skCircle(sketch, "E84", {"center": v(-203.2, 542.8) * mm, "radius": 47.63 * mm});
            skSolve(sketch);
        }
        {
            var Q0;
            Q0 = qSketchRegion(id + "F26", true);
            extrude(context, id + "F27", {"entities" : qUnion([Q0]), "operationType" : NewBodyOperationType.REMOVE, "endBound" : BoundingType.THROUGH_ALL, "oppositeDirection" : true, "depth" : 25.4 * mm});
        }
        {
            var Q0;
            Q0=makeQuery(id+"F1.opExtrude","CAP_FACE",FACE,{"disambiguationData":[OSD([sQuery(id+"F0.wireOp",EDGE,"E1.bottom"),sQuery(id+"F0.wireOp",EDGE,"E1.left"),sQuery(id+"F0.wireOp",EDGE,"E1.right"),sQuery(id+"F0.wireOp",EDGE,"E4.bottom"),sQuery(id+"F0.wireOp",EDGE,"E4.left"),sQuery(id+"F0.wireOp",EDGE,"E4.right"),sQuery(id+"F0.wireOp",EDGE,"E5.bottom"),sQuery(id+"F0.wireOp",EDGE,"E5.top"),sQuery(id+"F0.wireOp",EDGE,"E5.left"),sQuery(id+"F0.wireOp",EDGE,"E5.right"),sQuery(id+"F0.wireOp",EDGE,"E6.filletArc"),sQuery(id+"F0.wireOp",EDGE,"E7.filletArc"),sQuery(id+"F0.wireOp",EDGE,"E11"),sQuery(id+"F0.wireOp",EDGE,"E12"),sQuery(id+"F0.wireOp",EDGE,"E15.trimOffspring"),sQuery(id+"F0.wireOp",EDGE,"E16.trimOffspring")])],"isStart":true});
            var sketch = newSketch(context, id + "F28", { "sketchPlane" : qUnion([Q0])});
            skCircle(sketch, "E85.0", {"center": v(-203.2, 542.8) * mm, "radius": 47.63 * mm});
            skLineSegment(sketch, "E86.bottom", {"start": v(-298.45, 606.3) * mm, "end": v(-107.95, 606.3) * mm});
            skLineSegment(sketch, "E86.top", {"start": v(-298.45, 479.3) * mm, "end": v(-107.95, 479.3) * mm});
            skLineSegment(sketch, "E86.left", {"start": v(-298.45, 606.3) * mm, "end": v(-298.45, 479.3) * mm});
            skLineSegment(sketch, "E86.right", {"start": v(-107.95, 606.3) * mm, "end": v(-107.95, 479.3) * mm});
            skSolve(sketch);
        }
        {
            var Q0;
            Q0=makeQuery(id+"F28.imprint","IMPRINT",FACE,{"disambiguationData":[TD([[makeQuery(id+"F28.imprint","IMPRINT",EDGE,{"derivedFrom":sQuery(id+"F28.wireOp",EDGE,"E85.0")}),-1.0]])]});
            extrude(context, id + "F29", {"entities" : qUnion([Q0]), "operationType" : NewBodyOperationType.ADD, "depth" : 12.7 * mm});
        }
        {
            var Q0;
            Q0=makeQuery(id+"F29.opExtrude","CAP_FACE",FACE,{"disambiguationData":[OSD([sQuery(id+"F28.wireOp",EDGE,"E85.0"),sQuery(id+"F28.wireOp",EDGE,"E86.bottom"),sQuery(id+"F28.wireOp",EDGE,"E86.top"),sQuery(id+"F28.wireOp",EDGE,"E86.left"),sQuery(id+"F28.wireOp",EDGE,"E86.right")])],"isStart":false});
            var sketch = newSketch(context, id + "F30", { "sketchPlane" : qUnion([Q0])});
            skLineSegment(sketch, "E87", {"start": v(-203.2, 542.8) * mm, "end": v(-203.2, 441.36) * mm, "construction": true});
            skLineSegment(sketch, "E88", {"start": v(-203.2, 542.8) * mm, "end": v(-439.42, 542.8) * mm, "construction": true});
            skLineSegment(sketch, "E89.0", {"start": v(-203.2, 499.87) * mm, "end": v(-439.42, 499.87) * mm, "construction": true});
            skLineSegment(sketch, "E90.0", {"start": v(-276.35, 542.8) * mm, "end": v(-276.35, 441.36) * mm, "construction": true});
            skPoint(sketch, "E91", {"position": v(-276.35, 499.87) * mm});
            skPoint(sketch, "E92.MirrorP", {"position": v(-130.05, 499.87) * mm});
            skPoint(sketch, "E93.MirrorP", {"position": v(-276.35, 585.72) * mm});
            skPoint(sketch, "E94.MirrorP", {"position": v(-130.05, 585.72) * mm});
            skSolve(sketch);
        }
        {
            var Q0;
            Q0=sQuery(id+"F30.wireOp",VERTEX,"E93.MirrorP");
            var Q1;
            Q1=sQuery(id+"F30.wireOp",VERTEX,"E94.MirrorP");
            var Q2;
            Q2=sQuery(id+"F30.wireOp",VERTEX,"E92.MirrorP");
            var Q3;
            Q3=sQuery(id+"F30.wireOp",VERTEX,"E91");
            var Q4;
            Q4=makeQuery(id+"F1.opExtrude","SWEPT_BODY",BODY,{"disambiguationData":[OSD([sQuery(id+"F0.wireOp",EDGE,"E1.bottom"),sQuery(id+"F0.wireOp",EDGE,"E1.left"),sQuery(id+"F0.wireOp",EDGE,"E1.right"),sQuery(id+"F0.wireOp",EDGE,"E4.bottom"),sQuery(id+"F0.wireOp",EDGE,"E4.left"),sQuery(id+"F0.wireOp",EDGE,"E4.right"),sQuery(id+"F0.wireOp",EDGE,"E5.bottom"),sQuery(id+"F0.wireOp",EDGE,"E5.top"),sQuery(id+"F0.wireOp",EDGE,"E5.left"),sQuery(id+"F0.wireOp",EDGE,"E5.right"),sQuery(id+"F0.wireOp",EDGE,"E6.filletArc"),sQuery(id+"F0.wireOp",EDGE,"E7.filletArc"),sQuery(id+"F0.wireOp",EDGE,"E11"),sQuery(id+"F0.wireOp",EDGE,"E12"),sQuery(id+"F0.wireOp",EDGE,"E15.trimOffspring"),sQuery(id+"F0.wireOp",EDGE,"E16.trimOffspring")])]});
            hole(context, id + "F31", {"style" : HoleStyle.SIMPLE, "endStyle" : HoleEndStyle.BLIND, "standardTappedOrClearance" : lookupTablePath({ "standard" : "ANSI", "engagement" : "75%", "pitch" : "11 tpi", "size" : "5/8", "type" : "Tapped" }), "standardBlindInLast" : lookupTablePath({ "standard" : "ANSI", "engagement" : "75%", "pitch" : "11 tpi", "size" : "5/8", "type" : "Tapped" }), "holeDiameter" : 13.5 * mm, "showTappedDepth" : true, "holeDepth" : 31.75 * mm, "tappedDepth" : 24.82 * mm, "tapClearance" : 3, "startFromSketch" : true, "locations" : qUnion([Q0, Q1, Q2, Q3]), "scope" : qUnion([Q4]), "majorDiameter" : 15.88 * mm});
        }
    });
